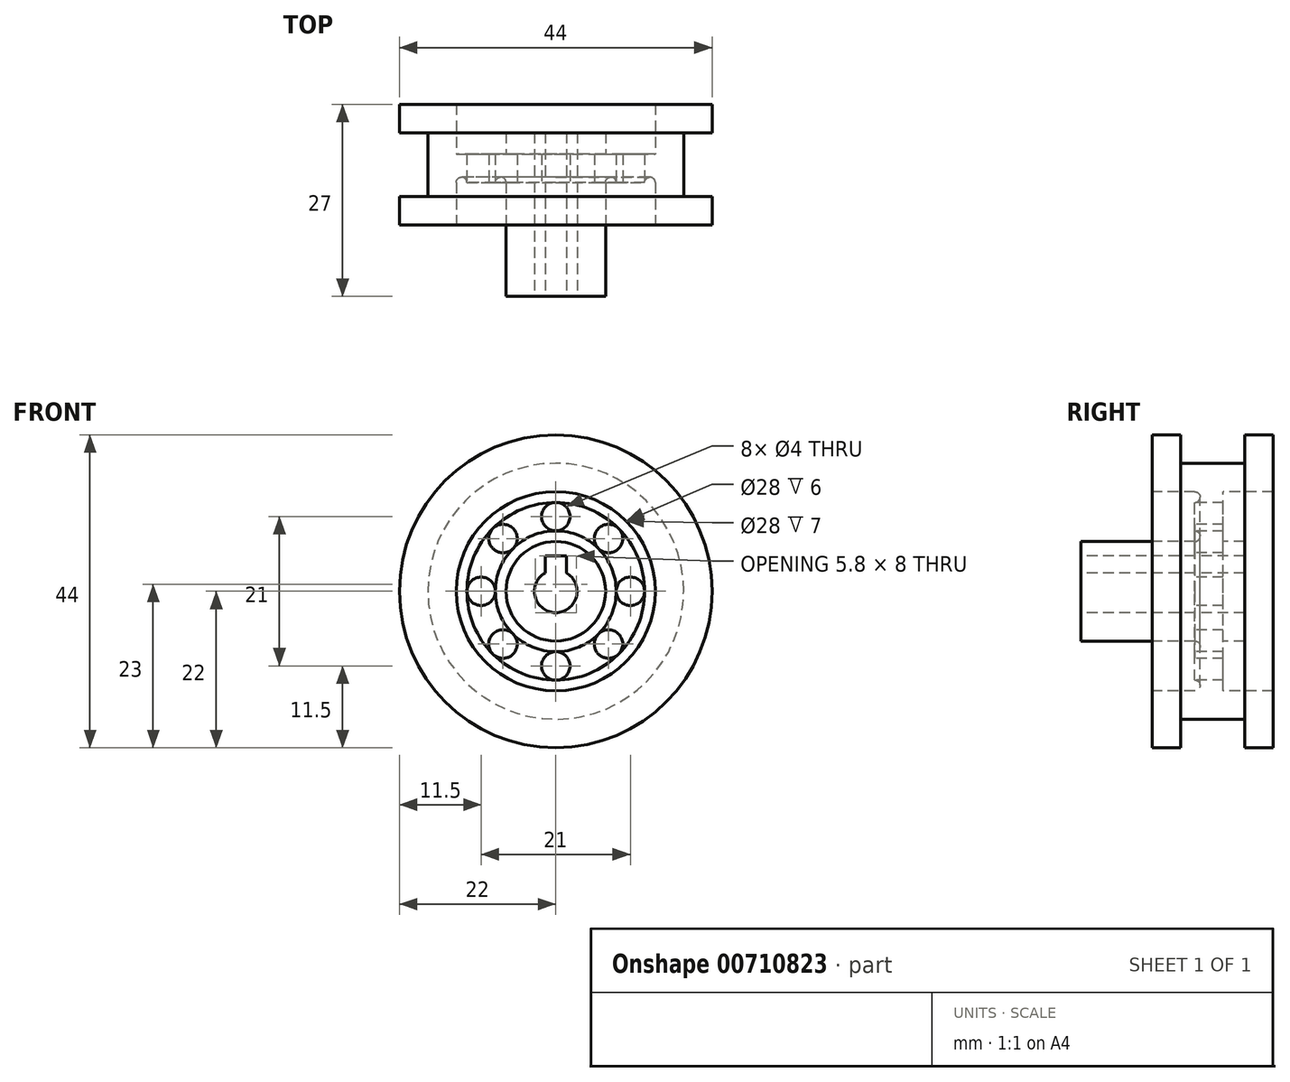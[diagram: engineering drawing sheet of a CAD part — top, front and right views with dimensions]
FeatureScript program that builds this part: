
annotation { "Feature Type Name" : "Feature", "Feature Type Description" : "" }
export const myFeature = defineFeature(function(context is Context, id is Id, definition is map)
    precondition{}
    {
        {
            var Q0;
            Q0=qCreatedBy(makeId("Right.planeOp"),FACE);
            var sketch = newSketch(context, id + "F0", { "sketchPlane" : qUnion([Q0])});
            skLineSegment(sketch, "E0", {"start": v(0, -3) * mm, "end": v(23, -3) * mm});
            skLineSegment(sketch, "E1", {"start": v(23, -3) * mm, "end": v(23, -7) * mm});
            skLineSegment(sketch, "E2", {"start": v(23, -7) * mm, "end": v(20, -7) * mm});
            skLineSegment(sketch, "E3", {"start": v(20, -7) * mm, "end": v(20, -14) * mm});
            skLineSegment(sketch, "E4", {"start": v(20, -14) * mm, "end": v(27, -14) * mm});
            skLineSegment(sketch, "E5", {"start": v(27, -14) * mm, "end": v(27, -22) * mm});
            skLineSegment(sketch, "E6", {"start": v(27, -22) * mm, "end": v(23, -22) * mm});
            skLineSegment(sketch, "E7", {"start": v(23, -22) * mm, "end": v(23, -18) * mm});
            skLineSegment(sketch, "E8", {"start": v(23, -18) * mm, "end": v(14, -18) * mm});
            skLineSegment(sketch, "E9", {"start": v(14, -18) * mm, "end": v(14, -22) * mm});
            skLineSegment(sketch, "E10", {"start": v(14, -22) * mm, "end": v(10, -22) * mm});
            skLineSegment(sketch, "E11", {"start": v(10, -22) * mm, "end": v(10, -14) * mm});
            skLineSegment(sketch, "E12", {"start": v(10, -14) * mm, "end": v(16, -14) * mm});
            skLineSegment(sketch, "E13", {"start": v(16, -14) * mm, "end": v(16, -7) * mm});
            skLineSegment(sketch, "E14", {"start": v(16, -7) * mm, "end": v(0, -7) * mm});
            skLineSegment(sketch, "E15", {"start": v(0, -7) * mm, "end": v(0, -3) * mm});
            skLineSegment(sketch, "E16", {"start": v(0, 0) * mm, "end": v(22.9, 0) * mm, "construction": true});
            skSolve(sketch);
        }
        {
            var Q0;
            Q0=makeQuery(id+"F0.imprint","IMPRINT",FACE,{"disambiguationData":[TD([[makeQuery(id+"F0.imprint","IMPRINT",EDGE,{"derivedFrom":sQuery(id+"F0.wireOp",EDGE,"E0")}),-1.0]])]});
            var Q1;
            Q1=sQuery(id+"F0.wireOp",EDGE,"E16");
            revolve(context, id + "F1", {"surfaceOperationType" : NewSurfaceOperationType.NEW, "entities" : qUnion([Q0]), "axis" : qUnion([Q1]), "revolveType" : RevolveType.FULL});
        }
        {
            var Q0;
            Q0=qCreatedBy(makeId("Front.planeOp"),FACE);
            var sketch = newSketch(context, id + "F2", { "sketchPlane" : qUnion([Q0])});
            skLineSegment(sketch, "E17", {"start": v(0, 0) * mm, "end": v(0, 5) * mm, "construction": true});
            skLineSegment(sketch, "E18.bottom", {"start": v(-1.5, 5) * mm, "end": v(1.5, 5) * mm});
            skLineSegment(sketch, "E18.left", {"start": v(-1.5, 5) * mm, "end": v(-1.5, 2.6) * mm});
            skLineSegment(sketch, "E18.right", {"start": v(1.5, 5) * mm, "end": v(1.5, 2.6) * mm});
            skPoint(sketch, "E19", {"position": v(0, 5) * mm});
            skLineSegment(sketch, "E20", {"start": v(-1.5, 2.6) * mm, "end": v(1.5, 2.6) * mm});
            skSolve(sketch);
        }
        {
            var Q0;
            Q0=makeQuery(id+"F1.opRevolve","SWEPT_FACE",FACE,{"disambiguationData":[OSD([sQuery(id+"F0.wireOp",EDGE,"E13")])]});
            var sketch = newSketch(context, id + "F3", { "sketchPlane" : qUnion([Q0])});
            skCircle(sketch, "E21", {"center": v(0, 10.5) * mm, "radius": 2 * mm});
            skCircle(sketch, "E22.1.0", {"center": v(7.42, 7.42) * mm, "radius": 2 * mm});
            skCircle(sketch, "E22.2.0", {"center": v(10.5, 0) * mm, "radius": 2 * mm});
            skCircle(sketch, "E22.3.0", {"center": v(7.42, -7.42) * mm, "radius": 2 * mm});
            skCircle(sketch, "E22.4.0", {"center": v(0, -10.5) * mm, "radius": 2 * mm});
            skCircle(sketch, "E22.5.0", {"center": v(-7.42, -7.42) * mm, "radius": 2 * mm});
            skCircle(sketch, "E22.6.0", {"center": v(-10.5, 0) * mm, "radius": 2 * mm});
            skCircle(sketch, "E22.7.0", {"center": v(-7.42, 7.42) * mm, "radius": 2 * mm});
            skPoint(sketch, "E22.center", {"position": v(0, 0) * mm});
            skLineSegment(sketch, "E22.anchor1", {"start": v(0, 0) * mm, "end": v(0, 10.5) * mm, "construction": true});
            skLineSegment(sketch, "E22.anchor2", {"start": v(0, 0) * mm, "end": v(-7.42, 7.42) * mm, "construction": true});
            skSolve(sketch);
        }
        {
            var Q0;
            Q0=makeQuery(id+"F2.imprint","IMPRINT",FACE,{"disambiguationData":[TD([[makeQuery(id+"F2.imprint","IMPRINT",EDGE,{"derivedFrom":sQuery(id+"F2.wireOp",EDGE,"E18.bottom")}),-1.0]])]});
            extrude(context, id + "F4", {"entities" : qUnion([Q0]), "operationType" : NewBodyOperationType.REMOVE, "endBound" : BoundingType.UP_TO_NEXT, "oppositeDirection" : true, "depth" : 25 * mm, "offsetDistance" : 25 * mm});
        }
        {
            var Q0;
            Q0 = qSketchRegion(id + "F3", true);
            extrude(context, id + "F5", {"entities" : qUnion([Q0]), "operationType" : NewBodyOperationType.REMOVE, "endBound" : BoundingType.UP_TO_NEXT, "oppositeDirection" : true, "depth" : 25 * mm, "offsetDistance" : 25 * mm});
        }
        {
            var Q0;
            Q0=makeQuery(id+"F1.opRevolve","SWEPT_FACE",FACE,{"disambiguationData":[OSD([sQuery(id+"F0.wireOp",EDGE,"E13")])]});
            var sketch = newSketch(context, id + "F6", { "sketchPlane" : qUnion([Q0])});
            skCircle(sketch, "E23", {"center": v(0, 0) * mm, "radius": 13.25 * mm});
            skSolve(sketch);
        }
        {
            var Q0;
            Q0=qCreatedBy(makeId("Top.planeOp"),FACE);
            var sketch = newSketch(context, id + "F7", { "sketchPlane" : qUnion([Q0])});
            skCircle(sketch, "E24", {"center": v(13.25, 16) * mm, "radius": 0.75 * mm});
            skSolve(sketch);
        }
        {
            var Q0;
            Q0 = qSketchRegion(id + "F7", true);
            var Q1;
            Q1=sQuery(id+"F6.wireOp",EDGE,"E23");
            sweep(context, id + "F8", {"operationType" : NewBodyOperationType.REMOVE, "profiles" : qUnion([Q0]), "path" : qUnion([Q1])});
        }
        {
            var Q0;
            Q0=qCreatedBy(makeId("Top.planeOp"),FACE);
            var sketch = newSketch(context, id + "F9", { "sketchPlane" : qUnion([Q0])});
            skCircle(sketch, "E25", {"center": v(7.75, 16) * mm, "radius": 0.75 * mm});
            skLineSegment(sketch, "E26", {"start": v(7, 16) * mm, "end": v(8.5, 16) * mm, "construction": true});
            skSolve(sketch);
        }
        {
            var Q0;
            Q0=makeQuery(id+"F1.opRevolve","SWEPT_FACE",FACE,{"disambiguationData":[OSD([sQuery(id+"F0.wireOp",EDGE,"E13")])]});
            var sketch = newSketch(context, id + "F10", { "sketchPlane" : qUnion([Q0])});
            skCircle(sketch, "E27", {"center": v(0, 0) * mm, "radius": 7.75 * mm});
            skSolve(sketch);
        }
        {
            var Q0;
            Q0 = qSketchRegion(id + "F9", true);
            var Q1;
            Q1 = qConstructionFilter(qBodyType(qCreatedBy(id + "F10" ,EDGE), BodyType.WIRE), ConstructionObject.NO);
            sweep(context, id + "F11", {"operationType" : NewBodyOperationType.REMOVE, "profiles" : qUnion([Q0]), "path" : qUnion([Q1])});
        }
    });
